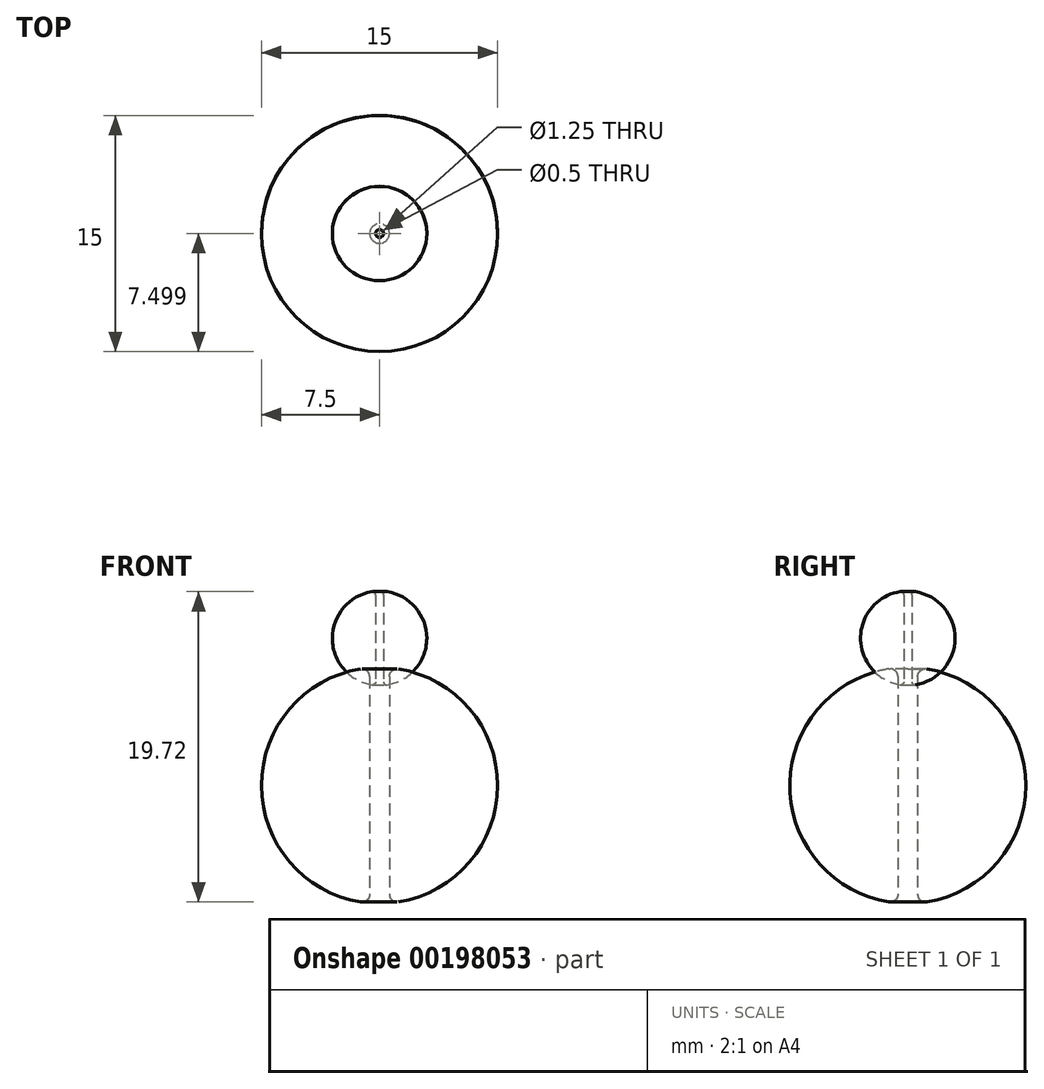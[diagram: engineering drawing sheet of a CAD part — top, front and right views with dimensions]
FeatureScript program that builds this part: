
annotation { "Feature Type Name" : "Feature", "Feature Type Description" : "" }
export const myFeature = defineFeature(function(context is Context, id is Id, definition is map)
    precondition{}
    {
        {
            var Q0;
            Q0=qCreatedBy(makeId("Top.planeOp"),FACE);
            var sketch = newSketch(context, id + "F0", { "sketchPlane" : qUnion([Q0])});
            skArc(sketch, "E0", {"start": v(3, 0.1) * mm, "mid": v(0, 3.1) * mm, "end": v(-3, 0.1) * mm});
            skCircle(sketch, "E1", {"center": v(0, 0.1) * mm, "radius": 0.25 * mm});
            skLineSegment(sketch, "E2", {"start": v(-3, 0.1) * mm, "end": v(3, 0.1) * mm});
            skSolve(sketch);
        }
        {
            var Q0;
            {var subQ0=sQuery(id+"F0.wireOp",EDGE,"E0");Q0=makeQuery(id+"F0.imprint","IMPRINT",FACE,{"disambiguationData":[TD([[makeQuery(id+"F0.imprint","IMPRINT",EDGE,{"derivedFrom":subQ0}),1.0]])]});}
            var Q1;
            Q1=sQuery(id+"F0.wireOp",EDGE,"E2");
            revolve(context, id + "F1", {"entities" : qUnion([Q0]), "axis" : qUnion([Q1]), "revolveType" : RevolveType.FULL});
        }
        {
            var Q0;
            {var subQ0=sQuery(id+"F0.wireOp",EDGE,"E2");var subQ1=sQuery(id+"F0.wireOp",EDGE,"E1");var subQ2=makeQuery(id+"F0.imprint","INTERSECT",VERTEX,{"disambiguationData":[OD(0.0)],"derivedFrom":[subQ1,subQ0]});Q0=makeQuery(id+"F0.imprint","IMPRINT",FACE,{"disambiguationData":[TD([[makeQuery(id+"F0.imprint","IMPRINT",EDGE,{"disambiguationData":[TD([[subQ2,-1.0]])],"derivedFrom":subQ1}),1.0]])]});}
            var Q1;
            {var subQ0=sQuery(id+"F0.wireOp",EDGE,"E2");var subQ1=sQuery(id+"F0.wireOp",EDGE,"E1");var subQ2=makeQuery(id+"F0.imprint","INTERSECT",VERTEX,{"disambiguationData":[OD(0.0)],"derivedFrom":[subQ1,subQ0]});Q1=makeQuery(id+"F0.imprint","IMPRINT",FACE,{"disambiguationData":[TD([[makeQuery(id+"F0.imprint","IMPRINT",EDGE,{"disambiguationData":[TD([[subQ2,1.0]])],"derivedFrom":subQ1}),1.0]])]});}
            extrude(context, id + "F2", {"entities" : qUnion([Q0, Q1]), "operationType" : NewBodyOperationType.REMOVE, "depth" : 25 * mm, "symmetric" : true});
        }
        {
            var Q0;
            Q0=makeQuery(id+"F2.boolean.opBoolean","INTERSECT",EDGE,{"disambiguationData":[OD(0.0)],"derivedFrom":[makeQuery(id+"F1.opRevolve","SWEPT_FACE",FACE,{"disambiguationData":[OSD([sQuery(id+"F0.wireOp",EDGE,"E0")])]}),makeQuery(id+"F2.opExtrude","SWEPT_FACE",FACE,{"disambiguationData":[OSD([sQuery(id+"F0.wireOp",EDGE,"E1")])]})]});
            var Q1;
            Q1=makeQuery(id+"F2.boolean.opBoolean","INTERSECT",EDGE,{"disambiguationData":[OD(1.0)],"derivedFrom":[makeQuery(id+"F1.opRevolve","SWEPT_FACE",FACE,{"disambiguationData":[OSD([sQuery(id+"F0.wireOp",EDGE,"E0")])]}),makeQuery(id+"F2.opExtrude","SWEPT_FACE",FACE,{"disambiguationData":[OSD([sQuery(id+"F0.wireOp",EDGE,"E1")])]})]});
            fillet(context, id + "F3", {"entities" : qUnion([Q0, Q1]), "radius" : .2 * mm, "allowEdgeOverflow" : false});
        }
        {
            var Q0;
            Q0=makeQuery(id+"F1.opRevolve","SWEPT_BODY",BODY,{"disambiguationData":[OSD([sQuery(id+"F0.wireOp",EDGE,"E0"),sQuery(id+"F0.wireOp",EDGE,"E1"),sQuery(id+"F0.wireOp",EDGE,"E2")])]});
            var Q1;
            Q1=sQuery(id+"F0.wireOp",VERTEX,"E1.center");
            transform(context, id + "F4", {"entities" : qUnion([Q0]), "transformType" : TransformType.SCALE_UNIFORMLY, "scale" : 2.5, "scalePoint" : qUnion([Q1]), "makeCopy" : true});
        }
        {
            var Q0;
            Q0=makeQuery(id+"F4.opPattern","COPY",BODY,{"derivedFrom":makeQuery(id+"F1.opRevolve","SWEPT_BODY",BODY,{"disambiguationData":[OSD([sQuery(id+"F0.wireOp",EDGE,"E0"),sQuery(id+"F0.wireOp",EDGE,"E1"),sQuery(id+"F0.wireOp",EDGE,"E2")])]}),"instanceName":"1"});
            transform(context, id + "F5", {"entities" : qUnion([Q0]), "transformType" : TransformType.TRANSLATION_3D, "dx" : 0 * mm, "dy" : 0 * mm, "dz" : -9.35 * mm, "makeCopy" : false});
        }
    });
